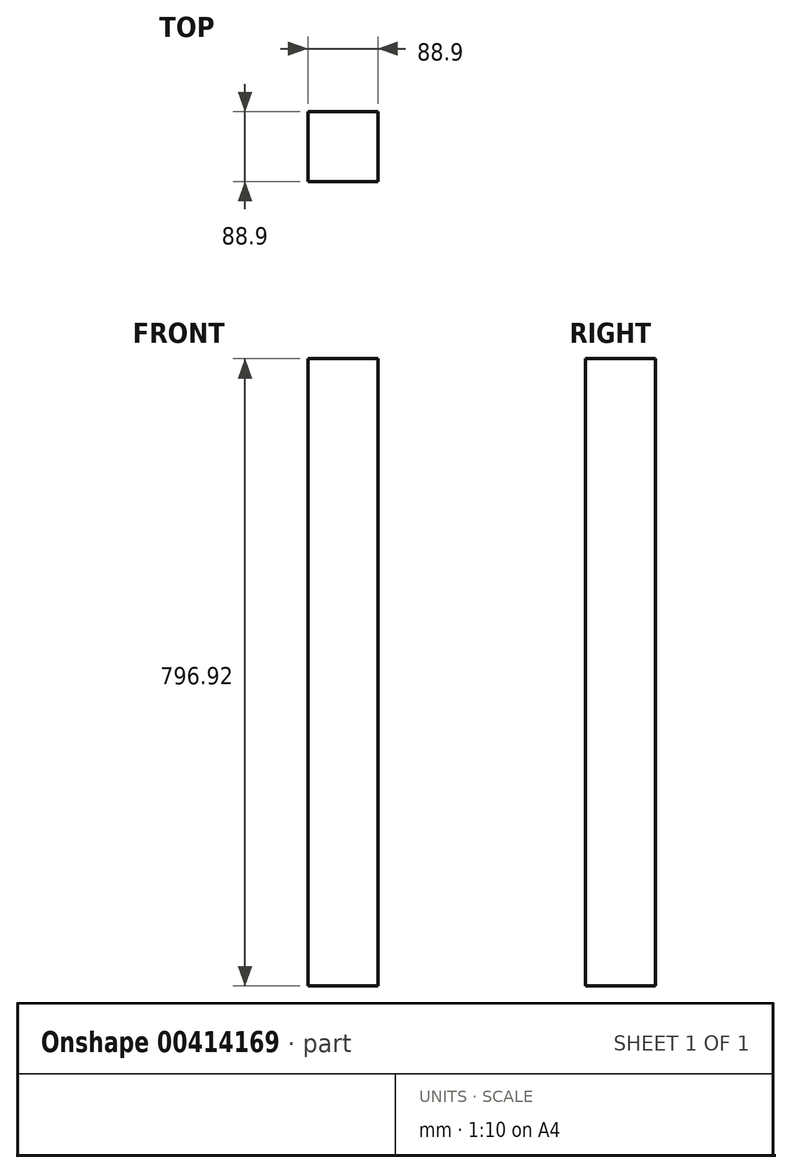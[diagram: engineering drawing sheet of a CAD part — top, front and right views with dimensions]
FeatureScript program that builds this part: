
annotation { "Feature Type Name" : "Feature", "Feature Type Description" : "" }
export const myFeature = defineFeature(function(context is Context, id is Id, definition is map)
    precondition{}
    {
        {
            var Q0;
            Q0=qCreatedBy(makeId("Top.planeOp"),FACE);
            var sketch = newSketch(context, id + "F0", { "sketchPlane" : qUnion([Q0])});
            skLineSegment(sketch, "E0.bottom", {"start": v(44.45, 44.45) * mm, "end": v(-44.45, 44.45) * mm});
            skLineSegment(sketch, "E0.top", {"start": v(44.45, -44.45) * mm, "end": v(-44.45, -44.45) * mm});
            skLineSegment(sketch, "E0.left", {"start": v(44.45, 44.45) * mm, "end": v(44.45, -44.45) * mm});
            skLineSegment(sketch, "E0.right", {"start": v(-44.45, 44.45) * mm, "end": v(-44.45, -44.45) * mm});
            skPoint(sketch, "E0.middle", {"position": v(0, 0) * mm});
            skSolve(sketch);
        }
        {
            var Q0;
            Q0=makeQuery(id+"F0.imprint","IMPRINT",FACE,{"disambiguationData":[TD([[makeQuery(id+"F0.imprint","IMPRINT",EDGE,{"derivedFrom":sQuery(id+"F0.wireOp",EDGE,"E0.bottom")}),1.0]])]});
            extrude(context, id + "F1", {"entities" : qUnion([Q0]), "endBound" : BoundingType.SYMMETRIC, "depth" : 796.92 * mm});
        }
    });
